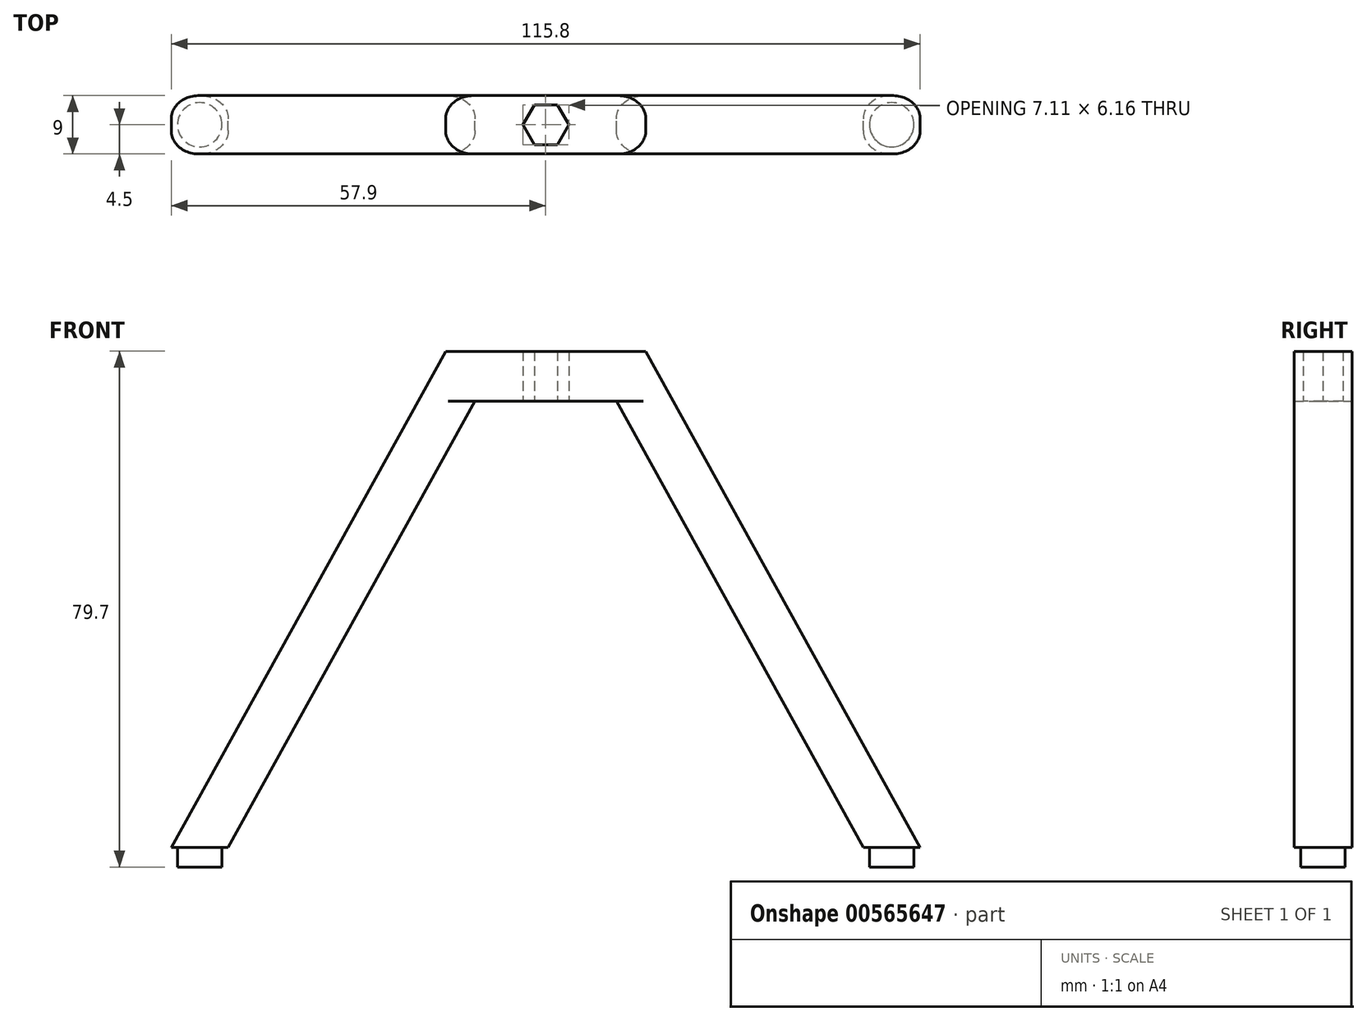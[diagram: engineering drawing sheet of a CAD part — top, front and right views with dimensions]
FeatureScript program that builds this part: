
annotation { "Feature Type Name" : "Feature", "Feature Type Description" : "" }
export const myFeature = defineFeature(function(context is Context, id is Id, definition is map)
    precondition{}
    {
        {
            var Q0;
            Q0=qCreatedBy(makeId("Front.planeOp"),FACE);
            var sketch = newSketch(context, id + "F0", { "sketchPlane" : qUnion([Q0])});
            skPoint(sketch, "E0.middle", {"position": v(0, 0) * mm});
            skLineSegment(sketch, "E1", {"start": v(0, 34.77) * mm, "end": v(10.93, 34.77) * mm});
            skLineSegment(sketch, "E2", {"start": v(0, 34.77) * mm, "end": v(-10.93, 34.77) * mm});
            skLineSegment(sketch, "E3", {"start": v(-10.93, 34.77) * mm, "end": v(-49.1, -34.23) * mm});
            skLineSegment(sketch, "E4", {"start": v(10.93, 34.77) * mm, "end": v(49.1, -34.23) * mm});
            skLineSegment(sketch, "E5.0", {"start": v(-15.47, 42.47) * mm, "end": v(-57.9, -34.23) * mm});
            skLineSegment(sketch, "E5.1", {"start": v(0, 42.47) * mm, "end": v(-15.47, 42.47) * mm});
            skLineSegment(sketch, "E5.2", {"start": v(0, 42.47) * mm, "end": v(15.47, 42.47) * mm});
            skLineSegment(sketch, "E5.3", {"start": v(15.47, 42.47) * mm, "end": v(57.9, -34.23) * mm});
            skLineSegment(sketch, "E6", {"start": v(-49.1, -34.23) * mm, "end": v(0, -34.23) * mm, "construction": true});
            skLineSegment(sketch, "E7", {"start": v(49.1, -34.23) * mm, "end": v(0, -34.23) * mm, "construction": true});
            skLineSegment(sketch, "E8", {"start": v(49.1, -34.23) * mm, "end": v(57.9, -34.23) * mm});
            skLineSegment(sketch, "E9", {"start": v(-49.1, -34.23) * mm, "end": v(-57.9, -34.23) * mm});
            skPoint(sketch, "E10", {"position": v(-53.5, -34.23) * mm});
            skPoint(sketch, "E11", {"position": v(53.5, -34.23) * mm});
            skLineSegment(sketch, "E12", {"start": v(0, -34.23) * mm, "end": v(0, 34.77) * mm, "construction": true});
            skLineSegment(sketch, "E13", {"start": v(-49.1, -34.23) * mm, "end": v(-53.5, -34.23) * mm, "construction": true});
            skSolve(sketch);
        }
        {
            var Q0;
            Q0=makeQuery(id+"F0.imprint","IMPRINT",FACE,{"disambiguationData":[TD([[makeQuery(id+"F0.imprint","IMPRINT",EDGE,{"derivedFrom":sQuery(id+"F0.wireOp",EDGE,"E1")}),1.0]])]});
            extrude(context, id + "F1", {"entities" : qUnion([Q0]), "depth" : 9 * mm, "offsetDistance" : 25 * mm});
        }
        {
            var Q0;
            Q0=makeQuery(id+"F1.opExtrude","SWEPT_FACE",FACE,{"disambiguationData":[OSD([sQuery(id+"F0.wireOp",EDGE,"E9")])]});
            var sketch = newSketch(context, id + "F2", { "sketchPlane" : qUnion([Q0])});
            skLineSegment(sketch, "E14", {"start": v(-57.9, 0) * mm, "end": v(-57.9, 9) * mm, "construction": true});
            skLineSegment(sketch, "E15", {"start": v(-57.9, 0) * mm, "end": v(-49.1, 0) * mm, "construction": true});
            skLineSegment(sketch, "E16", {"start": v(-57.9, 9) * mm, "end": v(-49.1, 9) * mm, "construction": true});
            skLineSegment(sketch, "E17", {"start": v(-49.1, 9) * mm, "end": v(-49.1, 0) * mm, "construction": true});
            skLineSegment(sketch, "E18", {"start": v(-57.9, 4.5) * mm, "end": v(-49.1, 4.5) * mm, "construction": true});
            skLineSegment(sketch, "E19", {"start": v(-53.5, 0) * mm, "end": v(-53.5, 9) * mm, "construction": true});
            skCircle(sketch, "E20", {"center": v(-53.5, 4.5) * mm, "radius": 3.43 * mm});
            skSolve(sketch);
        }
        {
            var Q0;
            Q0=makeQuery(id+"F1.opExtrude","SWEPT_FACE",FACE,{"disambiguationData":[OSD([sQuery(id+"F0.wireOp",EDGE,"E8")])]});
            var sketch = newSketch(context, id + "F3", { "sketchPlane" : qUnion([Q0])});
            skLineSegment(sketch, "E21", {"start": v(49.1, 9) * mm, "end": v(57.9, 9) * mm, "construction": true});
            skLineSegment(sketch, "E22", {"start": v(49.1, 9) * mm, "end": v(49.1, 0) * mm, "construction": true});
            skLineSegment(sketch, "E23", {"start": v(49.1, 0) * mm, "end": v(57.9, 0) * mm, "construction": true});
            skLineSegment(sketch, "E24", {"start": v(57.9, 9) * mm, "end": v(57.9, 0) * mm, "construction": true});
            skLineSegment(sketch, "E25", {"start": v(49.1, 4.5) * mm, "end": v(57.9, 4.5) * mm, "construction": true});
            skLineSegment(sketch, "E26", {"start": v(53.5, 9) * mm, "end": v(53.5, 0) * mm, "construction": true});
            skCircle(sketch, "E27", {"center": v(53.5, 4.5) * mm, "radius": 3.43 * mm});
            skSolve(sketch);
        }
        {
            var Q0;
            Q0=makeQuery(id+"F2.imprint","IMPRINT",FACE,{"disambiguationData":[TD([[makeQuery(id+"F2.imprint","IMPRINT",EDGE,{"derivedFrom":sQuery(id+"F2.wireOp",EDGE,"E20")}),1.0]])]});
            var Q1;
            Q1=makeQuery(id+"F3.imprint","IMPRINT",FACE,{"disambiguationData":[TD([[makeQuery(id+"F3.imprint","IMPRINT",EDGE,{"derivedFrom":sQuery(id+"F3.wireOp",EDGE,"E27")}),1.0]])]});
            extrude(context, id + "F4", {"entities" : qUnion([Q0, Q1]), "operationType" : NewBodyOperationType.ADD, "depth" : (6 / 2) * mm, "offsetDistance" : 25 * mm});
        }
        {
            var Q0;
            Q0=makeQuery(id+"F1.opExtrude","SWEPT_FACE",FACE,{"disambiguationData":[OSD([sQuery(id+"F0.wireOp",EDGE,"E1"),sQuery(id+"F0.wireOp",EDGE,"E2")])]});
            var sketch = newSketch(context, id + "F5", { "sketchPlane" : qUnion([Q0])});
            skLineSegment(sketch, "E28", {"start": v(-10.93, 9) * mm, "end": v(-10.93, 0) * mm, "construction": true});
            skLineSegment(sketch, "E29", {"start": v(-10.93, 0) * mm, "end": v(10.93, 0) * mm, "construction": true});
            skLineSegment(sketch, "E30", {"start": v(10.93, 9) * mm, "end": v(10.93, 0) * mm, "construction": true});
            skLineSegment(sketch, "E31", {"start": v(-10.93, 9) * mm, "end": v(10.93, 9) * mm, "construction": true});
            skLineSegment(sketch, "E32", {"start": v(0, 9) * mm, "end": v(0, 0) * mm, "construction": true});
            skLineSegment(sketch, "E33", {"start": v(-10.93, 4.5) * mm, "end": v(10.93, 4.5) * mm, "construction": true});
            skCircle(sketch, "E34.cCircle", {"center": v(0, 4.5) * mm, "radius": 3.56 * mm, "construction": true});
            skLineSegment(sketch, "E34.0", {"start": v(-3.56, 4.5) * mm, "end": v(-1.78, 7.58) * mm});
            skLineSegment(sketch, "E34.1", {"start": v(-1.78, 7.58) * mm, "end": v(1.78, 7.58) * mm});
            skLineSegment(sketch, "E34.2", {"start": v(1.78, 7.58) * mm, "end": v(3.56, 4.5) * mm});
            skLineSegment(sketch, "E34.3", {"start": v(3.56, 4.5) * mm, "end": v(1.78, 1.42) * mm});
            skLineSegment(sketch, "E34.4", {"start": v(1.78, 1.42) * mm, "end": v(-1.78, 1.42) * mm});
            skLineSegment(sketch, "E34.5", {"start": v(-1.78, 1.42) * mm, "end": v(-3.56, 4.5) * mm});
            skSolve(sketch);
        }
        {
            var Q0;
            Q0=makeQuery(id+"F5.imprint","IMPRINT",FACE,{"disambiguationData":[TD([[makeQuery(id+"F5.imprint","IMPRINT",EDGE,{"derivedFrom":sQuery(id+"F5.wireOp",EDGE,"E34.0")}),-1.0]])]});
            var Q1;
            Q1=makeQuery(id+"F1.opExtrude","SWEPT_FACE",FACE,{"disambiguationData":[OSD([sQuery(id+"F0.wireOp",EDGE,"E5.1"),sQuery(id+"F0.wireOp",EDGE,"E5.2")])]});
            extrude(context, id + "F6", {"entities" : qUnion([Q0]), "operationType" : NewBodyOperationType.REMOVE, "endBound" : BoundingType.UP_TO_SURFACE, "oppositeDirection" : true, "depth" : (15 / 2) * mm, "endBoundEntityFace" : qUnion([Q1]), "offsetDistance" : 25 * mm});
        }
        {
            var Q0;
            Q0=makeQuery(id+"F1.opExtrude","CAP_EDGE",EDGE,{"disambiguationData":[OSD([sQuery(id+"F0.wireOp",EDGE,"E5.0")])],"isStart":false});
            var Q1;
            Q1=makeQuery(id+"F1.opExtrude","CAP_EDGE",EDGE,{"disambiguationData":[OSD([sQuery(id+"F0.wireOp",EDGE,"E5.0")])],"isStart":true});
            var Q2;
            Q2=makeQuery(id+"F1.opExtrude","CAP_EDGE",EDGE,{"disambiguationData":[OSD([sQuery(id+"F0.wireOp",EDGE,"E5.3")])],"isStart":true});
            var Q3;
            Q3=makeQuery(id+"F1.opExtrude","CAP_EDGE",EDGE,{"disambiguationData":[OSD([sQuery(id+"F0.wireOp",EDGE,"E5.3")])],"isStart":false});
            var Q4;
            Q4=makeQuery(id+"F1.opExtrude","CAP_EDGE",EDGE,{"disambiguationData":[OSD([sQuery(id+"F0.wireOp",EDGE,"E3")])],"isStart":false});
            var Q5;
            Q5=makeQuery(id+"F1.opExtrude","CAP_EDGE",EDGE,{"disambiguationData":[OSD([sQuery(id+"F0.wireOp",EDGE,"E3")])],"isStart":true});
            var Q6;
            Q6=makeQuery(id+"F1.opExtrude","CAP_EDGE",EDGE,{"disambiguationData":[OSD([sQuery(id+"F0.wireOp",EDGE,"E4")])],"isStart":false});
            var Q7;
            Q7=makeQuery(id+"F1.opExtrude","CAP_EDGE",EDGE,{"disambiguationData":[OSD([sQuery(id+"F0.wireOp",EDGE,"E4")])],"isStart":true});
            fillet(context, id + "F7", {"entities" : qUnion([Q0, Q1, Q2, Q3, Q4, Q5, Q6, Q7]), "radius" : 3.62 * mm, "tangentPropagation" : true, "allowEdgeOverflow" : false});
        }
    });
